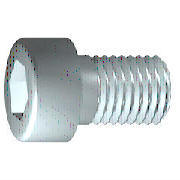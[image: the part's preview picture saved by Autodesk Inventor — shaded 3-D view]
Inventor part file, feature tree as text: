
AUTODESK INVENTOR PART (.ipt)
format: ipt  version: 2013 (Build 170138000, 138)  size: 194,048 bytes
history: native  units: mm (DEFAULTED — no unit token found)
features: sketch x2, extrude x1, plane x1, fillet x1
ambient origin geometry x7: Origin, YZ Plane, XY Plane, X Axis, Y Axis, Z Axis, Center Point
bodies: Solid1 (feature_tree), Body (feature_tree)
feature tree (5):
  extrude  "Slot"  Depth=1.5876mm
  plane  "Work Plane1"
  fillet  "Fillet2"  Radius=2.8448mm
  sketch  "Sketch1"  dims[d1=4.7623mm d2=1.5876mm d3=2.8448mm]
  sketch  "Sketch2"  dims[d4=1.2954mm d5=60.0deg d6=2.8448mm d7=2.8448mm d8=2.756963mm d9=4.6482mm d10=90.0deg d11=10.0mm d12=0.0mm d13=4.7623mm d14=0.0mm d15=0.37846mm d16=0.37846mm d17=0.2286mm d19=0.0mm d26=6.35mm d27=45.0deg d28=0.0mm d29=0.0mm d30=0.1016mm]
